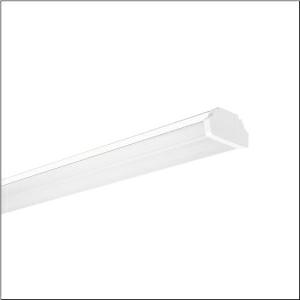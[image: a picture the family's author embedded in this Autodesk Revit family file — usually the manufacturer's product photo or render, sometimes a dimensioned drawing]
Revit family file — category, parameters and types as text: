
# Revit family: modario_31_gen_2_53bm812dv4a5c2_bb2c
name_source: partatom
category: Lighting Fixtures
units: mm (PartAtom-declared; Revit-internal decimal feet)

## family parameters
Cut with Voids When Loaded = No
Host = Face
Light Source = No
Part Type = Normal
Room Calculation Point = No
Round Connector Dimension = Use Diameter
Shared = No

## types (1)
- --- (1 x LED, 10860 lm, 61.4 W, 4000K)
    Apparent Load = 61 VA
    CIE Flux Codes = 47 80 95 93 100
    Color Rendering = 80
    Color Temperature = 4000K
    Default Elevation = 1800 mm
    Description = Modario 31 Gen.2, luminaire insert, of sheet steel, coil coated, white, length: 1.495mm, width: 81mm, height: 82mm, 5x system unit, system units: 299mm, LED rated luminous flux: 10.860lm, light colour: 840, SDCM (Standard Deviation of Colour Matching)MacAdam ≤ 3 SDCM (initial), control gear: DALI 2, control gear: ECG DALI, with plug, 5-pole, with phase selection, mains connection: 220..240V, AC, 50/60Hz, rated input power: 61W, through-wiring accessed according to module size, primary optical cover: cover, of PMMA, light emission: direct distribution, primary light characteristic: symmetric, protection rating (complete): IP20, protection rating (LED compartment): IP50, insulation class (complete): insulation class I (protective earthing), certification: CE, ENEC, VDE, UKCA, impact resistance: IK03, permissible ambient temperature for indoor applications: -25..+35°C, corresponds to IFS (International Featured Standards) requirements for safety and quality in the food industry, reducing of maximum allowable ambient temperature of 5°C with ceiling mounting, IP40 when using the optional accessory 5TP9018, packaging unit: 1 piece
    Height = 92 mm
    Lamp = 1 x LED
    Lamp Light Flux = 10860 lm
    Lamp Power = 61.4 W
    Lamp count = 1
    Length = 1495 mm
    Luminous efficacy = 177 lm/W
    Manufacturer = Siteco
    ModVariant = No
    Model = 53BM812DV4A5C2
    Mounting Place = Ceiling
    Mounting Type = Pendant
    Number of Poles = 1
    OnlyDefault = Yes
    Power Factor = 1
    Product Name = Modario 31 Gen.2
    Product group = luminaire insert | ceiling pendant
    ProductGroupID = 901
    Protection Class = Protection class I
    Protection Degree = IP 20
    RLX_Detail_Level = 1
    RLX_Emergency_Light_Flux = 0 lm
    RLX_Emergency_Type = 0
    RLX_Emergency_Type_DB = No
    RlxData = <blob elided: 42129 chars, md5=819b270b>
    Socket = socket
    Standby Power = 0 W
    System Light Flux = 10860 lm
    System Power = 61 W
    Type Comments = factory setting: luminous flux: 100 % | dim-lin: 254 | 418 mA
    Type Image = l_1341886.jpg
    URL = http://relux.com
    VarID = @adj_052707
    Voltage = 0 V
    Weight = 0.00 kg
    Width = 81 mm

## geometry (parser evidence)
native form markers: Blend x4, Sweep x13
no freeform markers — native parametric forms only
